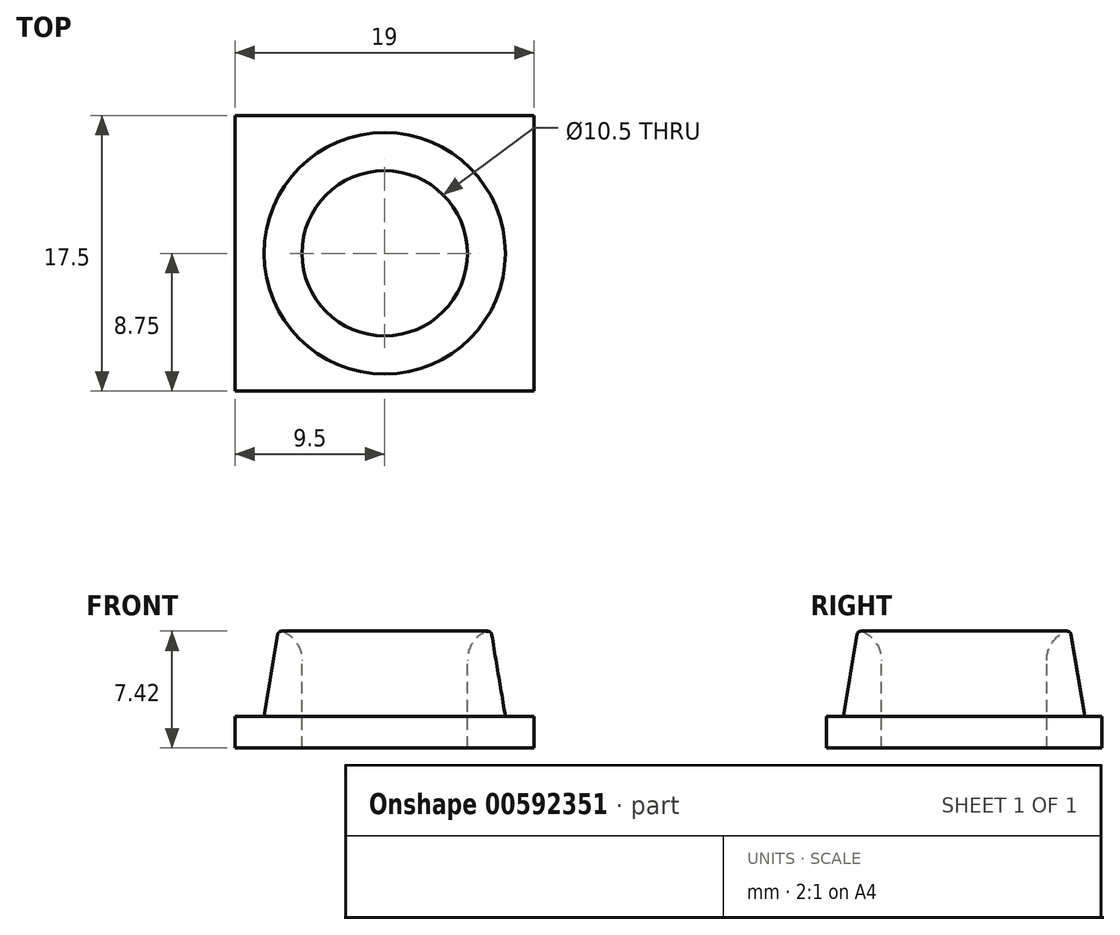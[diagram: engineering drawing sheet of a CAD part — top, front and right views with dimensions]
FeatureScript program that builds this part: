
annotation { "Feature Type Name" : "Feature", "Feature Type Description" : "" }
export const myFeature = defineFeature(function(context is Context, id is Id, definition is map)
    precondition{}
    {
        {
            var Q0;
            Q0=qCreatedBy(makeId("Top.planeOp"),FACE);
            var sketch = newSketch(context, id + "F0", { "sketchPlane" : qUnion([Q0])});
            skLineSegment(sketch, "E0.bottom", {"start": v(9.5, -8.75) * mm, "end": v(-9.5, -8.75) * mm});
            skLineSegment(sketch, "E0.top", {"start": v(9.5, 8.75) * mm, "end": v(-9.5, 8.75) * mm});
            skLineSegment(sketch, "E0.left", {"start": v(9.5, -8.75) * mm, "end": v(9.5, 8.75) * mm});
            skLineSegment(sketch, "E0.right", {"start": v(-9.5, -8.75) * mm, "end": v(-9.5, 8.75) * mm});
            skPoint(sketch, "E0.middle", {"position": v(0, 0) * mm});
            skSolve(sketch);
        }
        {
            var Q0;
            Q0=makeQuery(id+"F0.imprint","IMPRINT",FACE,{"disambiguationData":[TD([[makeQuery(id+"F0.imprint","IMPRINT",EDGE,{"derivedFrom":sQuery(id+"F0.wireOp",EDGE,"E0.bottom")}),-1.0]])]});
            extrude(context, id + "F1", {"entities" : qUnion([Q0]), "depth" : 2 * mm, "offsetDistance" : 25 * mm});
        }
        {
            var Q0;
            Q0=makeQuery(id+"F1.opExtrude","CAP_FACE",FACE,{"disambiguationData":[OSD([sQuery(id+"F0.wireOp",EDGE,"E0.bottom"),sQuery(id+"F0.wireOp",EDGE,"E0.top"),sQuery(id+"F0.wireOp",EDGE,"E0.left"),sQuery(id+"F0.wireOp",EDGE,"E0.right")])],"isStart":false});
            var sketch = newSketch(context, id + "F2", { "sketchPlane" : qUnion([Q0])});
            skCircle(sketch, "E1", {"center": v(0, 0) * mm, "radius": 5.25 * mm});
            skSolve(sketch);
        }
        {
            var Q0;
            Q0=makeQuery(id+"F2.imprint","IMPRINT",FACE,{"disambiguationData":[TD([[makeQuery(id+"F2.imprint","IMPRINT",EDGE,{"derivedFrom":sQuery(id+"F2.wireOp",EDGE,"E1")}),1.0]])]});
            extrude(context, id + "F3", {"entities" : qUnion([Q0]), "operationType" : NewBodyOperationType.REMOVE, "oppositeDirection" : true, "depth" : 2.5 * mm, "offsetDistance" : 25 * mm});
        }
        {
            var Q0;
            Q0=qCreatedBy(makeId("Front.planeOp"),FACE);
            var sketch = newSketch(context, id + "F4", { "sketchPlane" : qUnion([Q0])});
            skLineSegment(sketch, "E2", {"start": v(0, 0) * mm, "end": v(-5.25, 0) * mm, "construction": true});
            skLineSegment(sketch, "E3", {"start": v(-5.25, 0) * mm, "end": v(-5.25, 7.5) * mm});
            skLineSegment(sketch, "E4", {"start": v(-5.25, 7.5) * mm, "end": v(-6.75, 7.5) * mm});
            skPoint(sketch, "E5", {"position": v(-8, 0) * mm});
            skLineSegment(sketch, "E6", {"start": v(-8, 0) * mm, "end": v(-6.75, 7.5) * mm});
            skLineSegment(sketch, "E7", {"start": v(-8, 0) * mm, "end": v(-5.25, 0) * mm});
            skLineSegment(sketch, "E8", {"start": v(0, 0) * mm, "end": v(0, 15.23) * mm, "construction": true});
            skSolve(sketch);
        }
        {
            var Q0;
            Q0=makeQuery(id+"F4.imprint","IMPRINT",FACE,{"disambiguationData":[TD([[makeQuery(id+"F4.imprint","IMPRINT",EDGE,{"derivedFrom":sQuery(id+"F4.wireOp",EDGE,"E3")}),1.0]])]});
            var Q1;
            Q1=sQuery(id+"F4.wireOp",EDGE,"E8");
            revolve(context, id + "F5", {"operationType" : NewBodyOperationType.ADD, "entities" : qUnion([Q0]), "axis" : qUnion([Q1]), "revolveType" : RevolveType.FULL});
        }
        {
            var Q0;
            Q0=makeQuery(id+"F5.opRevolve","SWEPT_EDGE",EDGE,{"disambiguationData":[OSD([sQuery(id+"F4.wireOp",EDGE,"E3"),sQuery(id+"F4.wireOp",EDGE,"E4")])]});
            fillet(context, id + "F6", {"entities" : qUnion([Q0]), "radius" : 2 * mm, "tangentPropagation" : true, "allowEdgeOverflow" : false});
        }
        {
            var Q0;
            Q0=makeQuery(id+"F6.opFillet","BLEND_EDGE",EDGE,{"blendedFrom":[makeQuery(id+"F5.opRevolve","SWEPT_EDGE",EDGE,{"disambiguationData":[OSD([sQuery(id+"F4.wireOp",EDGE,"E3"),sQuery(id+"F4.wireOp",EDGE,"E4")])]}),makeQuery(id+"F5.opRevolve","SWEPT_FACE",FACE,{"disambiguationData":[OSD([sQuery(id+"F4.wireOp",EDGE,"E6")])]})],"blendedInto":[makeQuery(id+"F5.opRevolve","SWEPT_FACE",FACE,{"disambiguationData":[OSD([sQuery(id+"F4.wireOp",EDGE,"E6")])]})]});
            fillet(context, id + "F7", {"entities" : qUnion([Q0]), "radius" : .25 * mm, "tangentPropagation" : true, "allowEdgeOverflow" : false});
        }
    });
